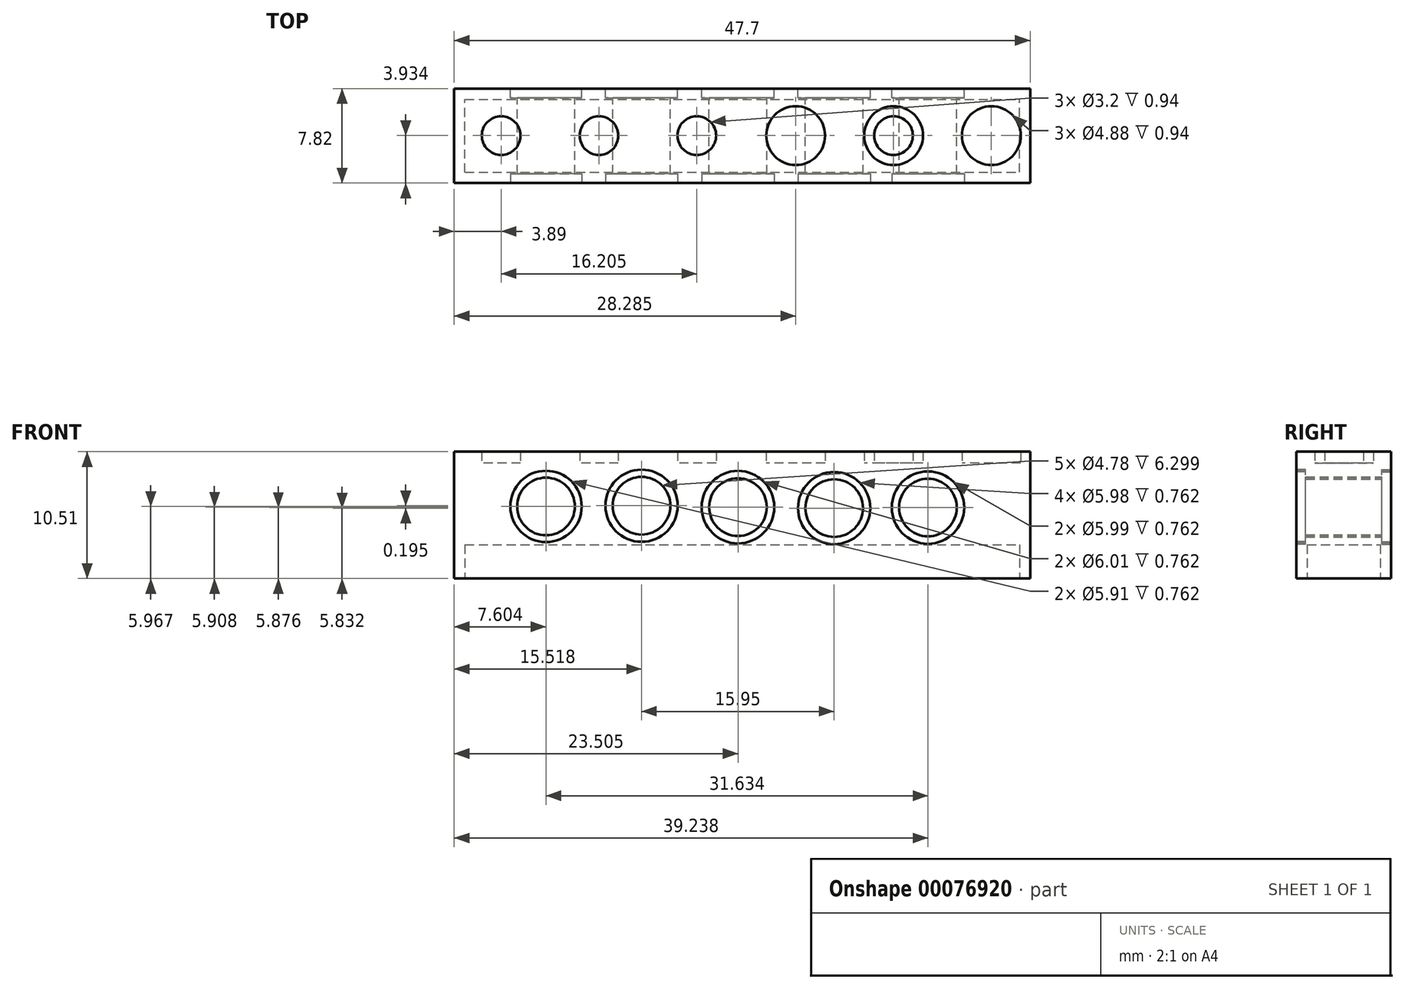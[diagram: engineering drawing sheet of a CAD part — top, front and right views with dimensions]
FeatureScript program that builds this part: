
annotation { "Feature Type Name" : "Feature", "Feature Type Description" : "" }
export const myFeature = defineFeature(function(context is Context, id is Id, definition is map)
    precondition{}
    {
        {
            var Q0;
            Q0=qCreatedBy(makeId("Front.planeOp"),FACE);
            var sketch = newSketch(context, id + "F0", { "sketchPlane" : qUnion([Q0])});
            skLineSegment(sketch, "E0.bottom", {"start": v(-24.19, 5.55) * mm, "end": v(23.51, 5.55) * mm});
            skLineSegment(sketch, "E0.top", {"start": v(-24.19, -4.02) * mm, "end": v(23.51, -4.02) * mm});
            skLineSegment(sketch, "E0.left", {"start": v(-24.19, 5.55) * mm, "end": v(-24.19, -4.02) * mm});
            skLineSegment(sketch, "E0.right", {"start": v(23.51, 5.55) * mm, "end": v(23.51, -4.02) * mm});
            skSolve(sketch);
        }
        {
            var Q0;
            Q0=makeQuery(id+"F0.imprint","IMPRINT",FACE,{"disambiguationData":[TD([[makeQuery(id+"F0.imprint","IMPRINT",EDGE,{"derivedFrom":sQuery(id+"F0.wireOp",EDGE,"E0.bottom")}),-1.0]])]});
            extrude(context, id + "F1", {"entities" : qUnion([Q0]), "depth" : 7.82 * mm});
        }
        {
            var Q0;
            Q0=qCreatedBy(makeId("Front.planeOp"),FACE);
            var sketch = newSketch(context, id + "F2", { "sketchPlane" : qUnion([Q0])});
            skLineSegment(sketch, "E1", {"start": v(-24.23, 2.32) * mm, "end": v(-19.4, 2.32) * mm});
            skLineSegment(sketch, "E2", {"start": v(-19.4, -3.88) * mm, "end": v(-19.4, -1) * mm});
            skLineSegment(sketch, "E3", {"start": v(-18.82, 5.6) * mm, "end": v(-18.82, 4.9) * mm});
            skLineSegment(sketch, "E4", {"start": v(-24.37, 4.9) * mm, "end": v(-16.52, 4.9) * mm});
            skLineSegment(sketch, "E5", {"start": v(-24.47, -1) * mm, "end": v(-16.62, -1) * mm});
            skCircle(sketch, "E6", {"center": v(-16.59, 1.95) * mm, "radius": 2.96 * mm});
            skPoint(sketch, "E6.second.point", {"position": v(-19.54, 1.92) * mm});
            skLineSegment(sketch, "E7", {"start": v(-16.52, 4.9) * mm, "end": v(-8.67, 4.9) * mm});
            skLineSegment(sketch, "E8", {"start": v(-16.62, -1) * mm, "end": v(-8.77, -1) * mm});
            skCircle(sketch, "E9", {"center": v(-8.67, 2) * mm, "radius": 2.99 * mm});
            skCircle(sketch, "E10", {"center": v(-0.69, 1.89) * mm, "radius": 3 * mm});
            skCircle(sketch, "E11", {"center": v(7.28, 1.81) * mm, "radius": 3 * mm});
            skCircle(sketch, "E12", {"center": v(15.05, 1.86) * mm, "radius": 3 * mm});
            skCircle(sketch, "E13", {"center": v(15.05, 1.86) * mm, "radius": 2.39 * mm});
            skCircle(sketch, "E14", {"center": v(7.28, 1.81) * mm, "radius": 2.39 * mm});
            skLineSegment(sketch, "E15", {"start": v(8.83, 3.62) * mm, "end": v(5.72, 0) * mm});
            skCircle(sketch, "E16", {"center": v(-0.69, 1.89) * mm, "radius": 2.39 * mm});
            skCircle(sketch, "E17", {"center": v(-8.67, 2) * mm, "radius": 2.39 * mm});
            skLineSegment(sketch, "E18", {"start": v(0.87, 3.7) * mm, "end": v(-2.24, 0.08) * mm});
            skLineSegment(sketch, "E19", {"start": v(-7.38, 4.02) * mm, "end": v(-9.96, 0) * mm});
            skCircle(sketch, "E20", {"center": v(-16.59, 1.95) * mm, "radius": 2.39 * mm});
            skLineSegment(sketch, "E21", {"start": v(-15.2, 3.9) * mm, "end": v(-17.97, 0) * mm});
            skSolve(sketch);
        }
        {
            var Q0;
            Q0=makeQuery(id+"F2.imprint","IMPRINT",FACE,{"disambiguationData":[TD([[makeQuery(id+"F2.imprint","IMPRINT",EDGE,{"derivedFrom":sQuery(id+"F2.wireOp",EDGE,"E13")}),1.0]])]});
            var Q1;
            {var subQ0=sQuery(id+"F2.wireOp",EDGE,"E15");Q1=makeQuery(id+"F2.imprint","IMPRINT",FACE,{"disambiguationData":[TD([[makeQuery(id+"F2.imprint","IMPRINT",EDGE,{"derivedFrom":subQ0}),-1.0]])]});}
            var Q2;
            {var subQ0=sQuery(id+"F2.wireOp",EDGE,"E15");Q2=makeQuery(id+"F2.imprint","IMPRINT",FACE,{"disambiguationData":[TD([[makeQuery(id+"F2.imprint","IMPRINT",EDGE,{"derivedFrom":subQ0}),1.0]])]});}
            var Q3;
            {var subQ0=sQuery(id+"F2.wireOp",EDGE,"E18");Q3=makeQuery(id+"F2.imprint","IMPRINT",FACE,{"disambiguationData":[TD([[makeQuery(id+"F2.imprint","IMPRINT",EDGE,{"derivedFrom":subQ0}),-1.0]])]});}
            var Q4;
            {var subQ0=sQuery(id+"F2.wireOp",EDGE,"E18");Q4=makeQuery(id+"F2.imprint","IMPRINT",FACE,{"disambiguationData":[TD([[makeQuery(id+"F2.imprint","IMPRINT",EDGE,{"derivedFrom":subQ0}),1.0]])]});}
            var Q5;
            {var subQ0=sQuery(id+"F2.wireOp",EDGE,"E19");Q5=makeQuery(id+"F2.imprint","IMPRINT",FACE,{"disambiguationData":[TD([[makeQuery(id+"F2.imprint","IMPRINT",EDGE,{"derivedFrom":subQ0}),-1.0]])]});}
            var Q6;
            {var subQ0=sQuery(id+"F2.wireOp",EDGE,"E19");Q6=makeQuery(id+"F2.imprint","IMPRINT",FACE,{"disambiguationData":[TD([[makeQuery(id+"F2.imprint","IMPRINT",EDGE,{"derivedFrom":subQ0}),1.0]])]});}
            var Q7;
            {var subQ0=sQuery(id+"F2.wireOp",EDGE,"E21");Q7=makeQuery(id+"F2.imprint","IMPRINT",FACE,{"disambiguationData":[TD([[makeQuery(id+"F2.imprint","IMPRINT",EDGE,{"derivedFrom":subQ0}),-1.0]])]});}
            var Q8;
            {var subQ0=sQuery(id+"F2.wireOp",EDGE,"E21");Q8=makeQuery(id+"F2.imprint","IMPRINT",FACE,{"disambiguationData":[TD([[makeQuery(id+"F2.imprint","IMPRINT",EDGE,{"derivedFrom":subQ0}),1.0]])]});}
            extrude(context, id + "F3", {"entities" : qUnion([Q0, Q1, Q2, Q3, Q4, Q5, Q6, Q7, Q8]), "operationType" : NewBodyOperationType.REMOVE, "depth" : 9.53 * mm});
        }
        {
            var Q0;
            {var subQ0=sQuery(id+"F2.wireOp",EDGE,"E6");var subQ1=sQuery(id+"F2.wireOp",EDGE,"E4");var subQ2=makeQuery(id+"F2.imprint","INTERSECT",VERTEX,{"disambiguationData":[OD(0.0)],"derivedFrom":[subQ1,subQ0]});Q0=makeQuery(id+"F2.imprint","IMPRINT",FACE,{"disambiguationData":[TD([[makeQuery(id+"F2.imprint","IMPRINT",EDGE,{"disambiguationData":[TD([[subQ2,1.0]])],"derivedFrom":subQ1}),1.0]])]});}
            var Q1;
            {var subQ0=sQuery(id+"F2.wireOp",EDGE,"E8");var subQ1=sQuery(id+"F2.wireOp",EDGE,"E6");var subQ2=makeQuery(id+"F2.imprint","INTERSECT",VERTEX,{"disambiguationData":[OD(0.0)],"derivedFrom":[subQ1,subQ0]});Q1=makeQuery(id+"F2.imprint","IMPRINT",FACE,{"disambiguationData":[TD([[makeQuery(id+"F2.imprint","IMPRINT",EDGE,{"disambiguationData":[TD([[subQ2,-1.0]])],"derivedFrom":subQ1}),1.0]])]});}
            var Q2;
            Q2=makeQuery(id+"F2.imprint","IMPRINT",FACE,{"disambiguationData":[TD([[makeQuery(id+"F2.imprint","IMPRINT",EDGE,{"derivedFrom":sQuery(id+"F2.wireOp",EDGE,"E12")}),1.0]])]});
            var Q3;
            Q3=makeQuery(id+"F2.imprint","IMPRINT",FACE,{"disambiguationData":[TD([[makeQuery(id+"F2.imprint","IMPRINT",EDGE,{"derivedFrom":sQuery(id+"F2.wireOp",EDGE,"E9")}),1.0]])]});
            var Q4;
            Q4=makeQuery(id+"F2.imprint","IMPRINT",FACE,{"disambiguationData":[TD([[makeQuery(id+"F2.imprint","IMPRINT",EDGE,{"derivedFrom":sQuery(id+"F2.wireOp",EDGE,"E10")}),1.0]])]});
            var Q5;
            Q5=makeQuery(id+"F2.imprint","IMPRINT",FACE,{"disambiguationData":[TD([[makeQuery(id+"F2.imprint","IMPRINT",EDGE,{"derivedFrom":sQuery(id+"F2.wireOp",EDGE,"E11")}),1.0]])]});
            var Q6;
            {var subQ0=sQuery(id+"F2.wireOp",EDGE,"E6");var subQ6=makeQuery(id+"F2.imprint","IMPRINT",VERTEX,{"derivedFrom":subQ0});Q6=makeQuery(id+"F2.imprint","IMPRINT",FACE,{"disambiguationData":[TD([[makeQuery(id+"F2.imprint","IMPRINT",EDGE,{"disambiguationData":[TD([[subQ6,1.0]])],"derivedFrom":subQ0}),1.0]])]});}
            extrude(context, id + "F4", {"entities" : qUnion([Q0, Q1, Q2, Q3, Q4, Q5, Q6]), "operationType" : NewBodyOperationType.REMOVE, "depth" : 0.76 * mm});
        }
        {
            var Q0;
            Q0=qCreatedBy(makeId("Front.planeOp"),FACE);
            var sketch = newSketch(context, id + "F5", { "sketchPlane" : qUnion([Q0])});
            skCircle(sketch, "E22.0", {"center": v(-16.59, 1.95) * mm, "radius": 2.96 * mm});
            skCircle(sketch, "E23.0", {"center": v(-8.67, 2) * mm, "radius": 2.99 * mm});
            skCircle(sketch, "E24.0", {"center": v(-0.69, 1.89) * mm, "radius": 3 * mm});
            skCircle(sketch, "E25.0.0", {"center": v(7.28, 1.81) * mm, "radius": 3 * mm});
            skCircle(sketch, "E26.0", {"center": v(15.05, 1.86) * mm, "radius": 3 * mm});
            skSolve(sketch);
        }
        {
            var Q0;
            Q0=makeQuery(id+"F5.imprint","IMPRINT",FACE,{"disambiguationData":[TD([[makeQuery(id+"F5.imprint","IMPRINT",EDGE,{"derivedFrom":sQuery(id+"F5.wireOp",EDGE,"E23.0")}),1.0]])]});
            var Q1;
            Q1=makeQuery(id+"F5.imprint","IMPRINT",FACE,{"disambiguationData":[TD([[makeQuery(id+"F5.imprint","IMPRINT",EDGE,{"derivedFrom":sQuery(id+"F5.wireOp",EDGE,"E24.0")}),1.0]])]});
            var Q2;
            Q2=makeQuery(id+"F5.imprint","IMPRINT",FACE,{"disambiguationData":[TD([[makeQuery(id+"F5.imprint","IMPRINT",EDGE,{"derivedFrom":sQuery(id+"F5.wireOp",EDGE,"E25.0.0")}),1.0]])]});
            var Q3;
            Q3=makeQuery(id+"F5.imprint","IMPRINT",FACE,{"disambiguationData":[TD([[makeQuery(id+"F5.imprint","IMPRINT",EDGE,{"derivedFrom":sQuery(id+"F5.wireOp",EDGE,"E26.0")}),1.0]])]});
            var Q4;
            Q4=makeQuery(id+"F5.imprint","IMPRINT",FACE,{"disambiguationData":[TD([[makeQuery(id+"F5.imprint","IMPRINT",EDGE,{"derivedFrom":sQuery(id+"F5.wireOp",EDGE,"E22.0")}),1.0]])]});
            extrude(context, id + "F6", {"entities" : qUnion([Q0, Q1, Q2, Q3, Q4]), "operationType" : NewBodyOperationType.REMOVE, "oppositeDirection" : true, "depth" : 25.4 * mm});
        }
        {
            var Q0;
            Q0=makeQuery(id+"F1.opExtrude","CAP_FACE",FACE,{"disambiguationData":[OSD([sQuery(id+"F0.wireOp",EDGE,"E0.bottom"),sQuery(id+"F0.wireOp",EDGE,"E0.top"),sQuery(id+"F0.wireOp",EDGE,"E0.left"),sQuery(id+"F0.wireOp",EDGE,"E0.right")])],"isStart":false});
            var sketch = newSketch(context, id + "F7", { "sketchPlane" : qUnion([Q0])});
            skLineSegment(sketch, "E27.0.0", {"start": v(23.51, 5.55) * mm, "end": v(-24.19, 5.55) * mm});
            skLineSegment(sketch, "E27.0.1", {"start": v(-24.19, 5.55) * mm, "end": v(-24.19, -4.02) * mm});
            skLineSegment(sketch, "E27.0.2", {"start": v(-24.19, -4.02) * mm, "end": v(23.51, -4.02) * mm});
            skLineSegment(sketch, "E27.0.3", {"start": v(23.51, -4.02) * mm, "end": v(23.51, 5.55) * mm});
            skCircle(sketch, "E28.0", {"center": v(15.05, 1.86) * mm, "radius": 3 * mm});
            skCircle(sketch, "E29.0", {"center": v(7.28, 1.81) * mm, "radius": 3 * mm});
            skCircle(sketch, "E30.0", {"center": v(-0.69, 1.89) * mm, "radius": 3 * mm});
            skCircle(sketch, "E31.0", {"center": v(-8.67, 2) * mm, "radius": 2.99 * mm});
            skCircle(sketch, "E32.0", {"center": v(-16.59, 1.95) * mm, "radius": 2.96 * mm});
            skCircle(sketch, "E33.0", {"center": v(-16.59, 1.95) * mm, "radius": 2.39 * mm});
            skCircle(sketch, "E34.0", {"center": v(-8.67, 2) * mm, "radius": 2.39 * mm});
            skCircle(sketch, "E35.0", {"center": v(-0.69, 1.89) * mm, "radius": 2.39 * mm});
            skCircle(sketch, "E36.0", {"center": v(7.28, 1.81) * mm, "radius": 2.39 * mm});
            skCircle(sketch, "E37.0", {"center": v(15.05, 1.86) * mm, "radius": 2.39 * mm});
            skSolve(sketch);
        }
        {
            var Q0;
            Q0=makeQuery(id+"F7.imprint","IMPRINT",FACE,{"disambiguationData":[TD([[makeQuery(id+"F7.imprint","IMPRINT",EDGE,{"derivedFrom":sQuery(id+"F7.wireOp",EDGE,"E30.0")}),1.0]])]});
            var Q1;
            Q1=makeQuery(id+"F7.imprint","IMPRINT",FACE,{"disambiguationData":[TD([[makeQuery(id+"F7.imprint","IMPRINT",EDGE,{"derivedFrom":sQuery(id+"F7.wireOp",EDGE,"E29.0")}),1.0]])]});
            var Q2;
            Q2=makeQuery(id+"F7.imprint","IMPRINT",FACE,{"disambiguationData":[TD([[makeQuery(id+"F7.imprint","IMPRINT",EDGE,{"derivedFrom":sQuery(id+"F7.wireOp",EDGE,"E28.0")}),1.0]])]});
            var Q3;
            Q3=makeQuery(id+"F7.imprint","IMPRINT",FACE,{"disambiguationData":[TD([[makeQuery(id+"F7.imprint","IMPRINT",EDGE,{"derivedFrom":sQuery(id+"F7.wireOp",EDGE,"E34.0")}),-1.0]])]});
            var Q4;
            Q4=makeQuery(id+"F7.imprint","IMPRINT",FACE,{"disambiguationData":[TD([[makeQuery(id+"F7.imprint","IMPRINT",EDGE,{"derivedFrom":sQuery(id+"F7.wireOp",EDGE,"E32.0")}),1.0]])]});
            var Q5;
            Q5=makeQuery(id+"F7.imprint","IMPRINT",FACE,{"disambiguationData":[TD([[makeQuery(id+"F7.imprint","IMPRINT",EDGE,{"derivedFrom":sQuery(id+"F7.wireOp",EDGE,"E31.0")}),1.0]])]});
            extrude(context, id + "F8", {"entities" : qUnion([Q0, Q1, Q2, Q3, Q4, Q5]), "operationType" : NewBodyOperationType.REMOVE, "oppositeDirection" : true, "depth" : 0.76 * mm});
        }
        {
            var Q0;
            Q0=makeQuery(id+"F1.opExtrude","SWEPT_FACE",FACE,{"disambiguationData":[OSD([sQuery(id+"F0.wireOp",EDGE,"E0.bottom")])]});
            var sketch = newSketch(context, id + "F9", { "sketchPlane" : qUnion([Q0])});
            skCircle(sketch, "E38", {"center": v(-20.3, -3.89) * mm, "radius": 1.6 * mm});
            skCircle(sketch, "E39", {"center": v(-20.3, -3.89) * mm, "radius": 2.44 * mm});
            skCircle(sketch, "E40", {"center": v(-12.2, -3.89) * mm, "radius": 1.6 * mm});
            skCircle(sketch, "E41", {"center": v(-12.2, -3.89) * mm, "radius": 2.44 * mm});
            skCircle(sketch, "E42", {"center": v(-4.1, -3.89) * mm, "radius": 1.6 * mm});
            skCircle(sketch, "E43", {"center": v(-4.1, -3.89) * mm, "radius": 2.44 * mm});
            skLineSegment(sketch, "E44.0.0", {"start": v(23.51, 0) * mm, "end": v(-24.19, 0) * mm});
            skLineSegment(sketch, "E44.0.1", {"start": v(-24.19, 0) * mm, "end": v(-24.19, -7.82) * mm});
            skLineSegment(sketch, "E44.0.2", {"start": v(-24.19, -7.82) * mm, "end": v(23.51, -7.82) * mm});
            skLineSegment(sketch, "E44.0.3", {"start": v(23.51, -7.82) * mm, "end": v(23.51, 0) * mm});
            skLineSegment(sketch, "E45.0", {"start": v(-24.19, 0) * mm, "end": v(23.51, 0) * mm});
            skCircle(sketch, "E46.MirrorC", {"center": v(4.1, -3.89) * mm, "radius": 2.44 * mm});
            skCircle(sketch, "E47.MirrorC", {"center": v(4.1, -3.89) * mm, "radius": 1.6 * mm});
            skCircle(sketch, "E48.MirrorC", {"center": v(12.2, -3.89) * mm, "radius": 1.6 * mm});
            skCircle(sketch, "E49.MirrorC", {"center": v(12.2, -3.89) * mm, "radius": 2.44 * mm});
            skCircle(sketch, "E50.MirrorC", {"center": v(20.3, -3.89) * mm, "radius": 2.44 * mm});
            skCircle(sketch, "E51.MirrorC", {"center": v(20.3, -3.89) * mm, "radius": 1.6 * mm});
            skSolve(sketch);
        }
        {
            var Q0;
            Q0=makeQuery(id+"F9.imprint","IMPRINT",FACE,{"disambiguationData":[TD([[makeQuery(id+"F9.imprint","IMPRINT",EDGE,{"derivedFrom":sQuery(id+"F9.wireOp",EDGE,"E38")}),-1.0]])]});
            var Q1;
            Q1=makeQuery(id+"F9.imprint","IMPRINT",FACE,{"disambiguationData":[TD([[makeQuery(id+"F9.imprint","IMPRINT",EDGE,{"derivedFrom":sQuery(id+"F9.wireOp",EDGE,"E40")}),-1.0]])]});
            var Q2;
            Q2=makeQuery(id+"F9.imprint","IMPRINT",FACE,{"disambiguationData":[TD([[makeQuery(id+"F9.imprint","IMPRINT",EDGE,{"derivedFrom":sQuery(id+"F9.wireOp",EDGE,"E42")}),-1.0]])]});
            var Q3;
            Q3=makeQuery(id+"F9.imprint","IMPRINT",FACE,{"disambiguationData":[TD([[makeQuery(id+"F9.imprint","IMPRINT",EDGE,{"derivedFrom":sQuery(id+"F9.wireOp",EDGE,"E46.MirrorC")}),-1.0]])]});
            var Q4;
            Q4=makeQuery(id+"F9.imprint","IMPRINT",FACE,{"disambiguationData":[TD([[makeQuery(id+"F9.imprint","IMPRINT",EDGE,{"derivedFrom":sQuery(id+"F9.wireOp",EDGE,"E48.MirrorC")}),1.0]])]});
            var Q5;
            Q5=makeQuery(id+"F9.imprint","IMPRINT",FACE,{"disambiguationData":[TD([[makeQuery(id+"F9.imprint","IMPRINT",EDGE,{"derivedFrom":sQuery(id+"F9.wireOp",EDGE,"E50.MirrorC")}),-1.0]])]});
            extrude(context, id + "F10", {"entities" : qUnion([Q0, Q1, Q2, Q3, Q4, Q5]), "operationType" : NewBodyOperationType.ADD, "depth" : 0.94 * mm});
        }
        {
            var Q0;
            Q0=makeQuery(id+"F1.opExtrude","SWEPT_FACE",FACE,{"disambiguationData":[OSD([sQuery(id+"F0.wireOp",EDGE,"E0.top")])]});
            var sketch = newSketch(context, id + "F11", { "sketchPlane" : qUnion([Q0])});
            skLineSegment(sketch, "E52.bottom", {"start": v(-23.3, 6.93) * mm, "end": v(22.63, 6.93) * mm});
            skLineSegment(sketch, "E52.top", {"start": v(-23.3, 0.89) * mm, "end": v(22.63, 0.89) * mm});
            skLineSegment(sketch, "E52.left", {"start": v(-23.3, 6.93) * mm, "end": v(-23.3, 0.89) * mm});
            skLineSegment(sketch, "E52.right", {"start": v(22.63, 6.93) * mm, "end": v(22.63, 0.89) * mm});
            skSolve(sketch);
        }
        {
            var Q0;
            Q0=makeQuery(id+"F11.imprint","IMPRINT",FACE,{"disambiguationData":[TD([[makeQuery(id+"F11.imprint","IMPRINT",EDGE,{"derivedFrom":sQuery(id+"F11.wireOp",EDGE,"E52.bottom")}),-1.0]])]});
            extrude(context, id + "F12", {"entities" : qUnion([Q0]), "operationType" : NewBodyOperationType.REMOVE, "oppositeDirection" : true, "depth" : 2.8 * mm});
        }
    });
